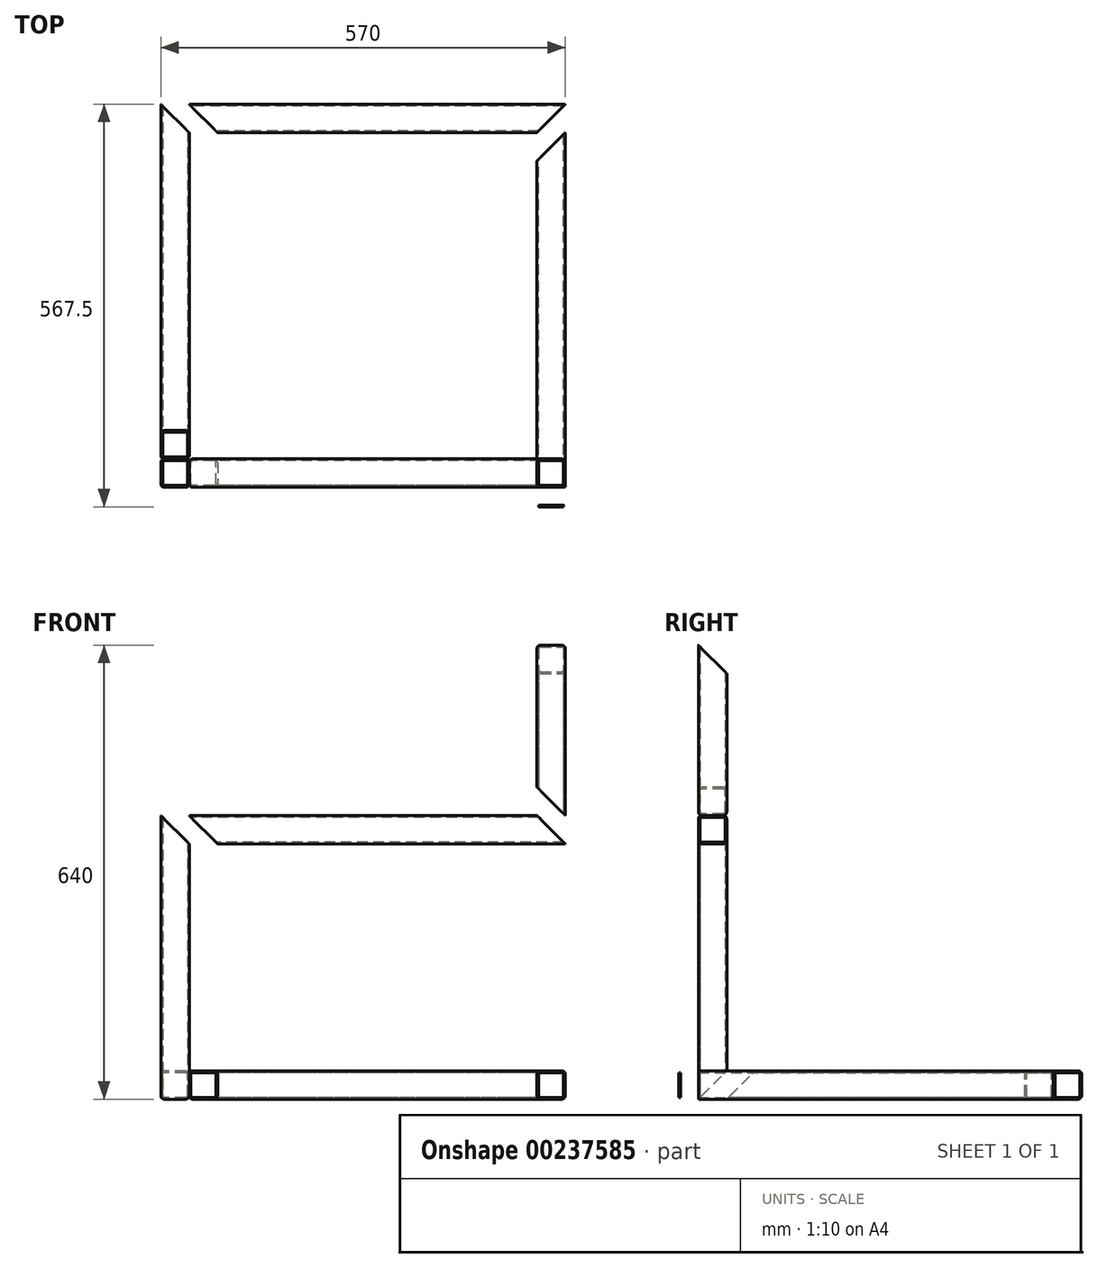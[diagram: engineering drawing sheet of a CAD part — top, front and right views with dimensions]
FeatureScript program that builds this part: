
annotation { "Feature Type Name" : "Feature", "Feature Type Description" : "" }
export const myFeature = defineFeature(function(context is Context, id is Id, definition is map)
    precondition{}
    {
        {
            var Q0;
            Q0=qCreatedBy(makeId("Front.planeOp"),FACE);
            var sketch = newSketch(context, id + "F0", { "sketchPlane" : qUnion([Q0])});
            skLineSegment(sketch, "E0.bottom", {"start": v(5, 0) * mm, "end": v(35, 0) * mm});
            skLineSegment(sketch, "E0.top", {"start": v(5, 40) * mm, "end": v(35, 40) * mm});
            skLineSegment(sketch, "E0.left", {"start": v(0, 5) * mm, "end": v(0, 35) * mm});
            skLineSegment(sketch, "E0.right", {"start": v(40, 5) * mm, "end": v(40, 35) * mm});
            skPoint(sketch, "E1.visualSharp", {"position": v(0, 0) * mm});
            skArc(sketch, "E1.filletArc", {"start": v(0, 5) * mm, "mid": v(1.46, 1.46) * mm, "end": v(5, 0) * mm});
            skPoint(sketch, "E2.visualSharp", {"position": v(0, 40) * mm});
            skArc(sketch, "E2.filletArc", {"start": v(5, 40) * mm, "mid": v(1.46, 38.54) * mm, "end": v(0, 35) * mm});
            skPoint(sketch, "E3.visualSharp", {"position": v(40, 40) * mm});
            skArc(sketch, "E3.filletArc", {"start": v(40, 35) * mm, "mid": v(38.54, 38.54) * mm, "end": v(35, 40) * mm});
            skPoint(sketch, "E4.visualSharp", {"position": v(40, 0) * mm});
            skArc(sketch, "E4.filletArc", {"start": v(35, 0) * mm, "mid": v(38.54, 1.46) * mm, "end": v(40, 5) * mm});
            skLineSegment(sketch, "E5.0", {"start": v(5, 37.5) * mm, "end": v(35, 37.5) * mm});
            skLineSegment(sketch, "E5.1", {"start": v(2.5, 5) * mm, "end": v(2.5, 35) * mm});
            skLineSegment(sketch, "E5.2", {"start": v(5, 2.5) * mm, "end": v(35, 2.5) * mm});
            skLineSegment(sketch, "E5.3", {"start": v(37.5, 5) * mm, "end": v(37.5, 35) * mm});
            skPoint(sketch, "E6.visualSharp", {"position": v(37.5, 37.5) * mm});
            skArc(sketch, "E6.filletArc", {"start": v(37.5, 35) * mm, "mid": v(36.77, 36.77) * mm, "end": v(35, 37.5) * mm});
            skPoint(sketch, "E7.visualSharp", {"position": v(2.5, 37.5) * mm});
            skArc(sketch, "E7.filletArc", {"start": v(5, 37.5) * mm, "mid": v(3.23, 36.77) * mm, "end": v(2.5, 35) * mm});
            skPoint(sketch, "E8.visualSharp", {"position": v(2.5, 2.5) * mm});
            skArc(sketch, "E8.filletArc", {"start": v(2.5, 5) * mm, "mid": v(3.23, 3.23) * mm, "end": v(5, 2.5) * mm});
            skPoint(sketch, "E9.visualSharp", {"position": v(37.5, 2.5) * mm});
            skArc(sketch, "E9.filletArc", {"start": v(35, 2.5) * mm, "mid": v(36.77, 3.23) * mm, "end": v(37.5, 5) * mm});
            skSolve(sketch);
        }
        {
            var Q0;
            Q0=makeQuery(id+"F0.imprint","IMPRINT",FACE,{"disambiguationData":[TD([[makeQuery(id+"F0.imprint","IMPRINT",EDGE,{"derivedFrom":sQuery(id+"F0.wireOp",EDGE,"E0.bottom")}),1.0]])]});
            extrude(context, id + "F1", {"entities" : qUnion([Q0]), "oppositeDirection" : true, "depth" : 500 * mm});
        }
        {
            var Q0;
            Q0=makeQuery(id+"F1.opExtrude","SWEPT_FACE",FACE,{"disambiguationData":[OSD([sQuery(id+"F0.wireOp",EDGE,"E0.top")])]});
            var sketch = newSketch(context, id + "F2", { "sketchPlane" : qUnion([Q0])});
            skLineSegment(sketch, "E10", {"start": v(40, 500) * mm, "end": v(0, 500) * mm});
            skLineSegment(sketch, "E11", {"start": v(0, 500) * mm, "end": v(0, 460) * mm});
            skLineSegment(sketch, "E12", {"start": v(0, 460) * mm, "end": v(40, 500) * mm});
            skSolve(sketch);
        }
        {
            var Q0;
            Q0 = qSketchRegion(id + "F2", true);
            extrude(context, id + "F3", {"entities" : qUnion([Q0]), "operationType" : NewBodyOperationType.REMOVE, "endBound" : BoundingType.THROUGH_ALL, "oppositeDirection" : true, "depth" : 25 * mm});
        }
        {
            var Q0;
            Q0=qCreatedBy(makeId("Front.planeOp"),FACE);
            var sketch = newSketch(context, id + "F4", { "sketchPlane" : qUnion([Q0])});
            skLineSegment(sketch, "E13.bottom", {"start": v(-227.11, 224.23) * mm, "end": v(-197.11, 224.23) * mm});
            skLineSegment(sketch, "E13.top", {"start": v(-227.11, 264.23) * mm, "end": v(-197.11, 264.23) * mm});
            skLineSegment(sketch, "E13.left", {"start": v(-232.11, 229.23) * mm, "end": v(-232.11, 259.23) * mm});
            skLineSegment(sketch, "E13.right", {"start": v(-192.11, 229.23) * mm, "end": v(-192.11, 259.23) * mm});
            skPoint(sketch, "E14.visualSharp", {"position": v(-232.11, 224.23) * mm});
            skArc(sketch, "E14.filletArc", {"start": v(-232.11, 229.23) * mm, "mid": v(-230.65, 225.7) * mm, "end": v(-227.11, 224.23) * mm});
            skPoint(sketch, "E15.visualSharp", {"position": v(-232.11, 264.23) * mm});
            skArc(sketch, "E15.filletArc", {"start": v(-227.11, 264.23) * mm, "mid": v(-230.65, 262.77) * mm, "end": v(-232.11, 259.23) * mm});
            skPoint(sketch, "E16.visualSharp", {"position": v(-192.11, 264.23) * mm});
            skArc(sketch, "E16.filletArc", {"start": v(-192.11, 259.23) * mm, "mid": v(-193.57, 262.77) * mm, "end": v(-197.11, 264.23) * mm});
            skPoint(sketch, "E17.visualSharp", {"position": v(-192.11, 224.23) * mm});
            skArc(sketch, "E17.filletArc", {"start": v(-197.11, 224.23) * mm, "mid": v(-193.57, 225.7) * mm, "end": v(-192.11, 229.23) * mm});
            skLineSegment(sketch, "E18.0", {"start": v(-227.11, 261.73) * mm, "end": v(-197.11, 261.73) * mm});
            skLineSegment(sketch, "E18.1", {"start": v(-229.61, 229.23) * mm, "end": v(-229.61, 259.23) * mm});
            skLineSegment(sketch, "E18.2", {"start": v(-227.11, 226.73) * mm, "end": v(-197.11, 226.73) * mm});
            skLineSegment(sketch, "E18.3", {"start": v(-194.61, 229.23) * mm, "end": v(-194.61, 259.23) * mm});
            skPoint(sketch, "E19.visualSharp", {"position": v(-194.61, 261.73) * mm});
            skArc(sketch, "E19.filletArc", {"start": v(-194.61, 259.23) * mm, "mid": v(-195.34, 261) * mm, "end": v(-197.11, 261.73) * mm});
            skPoint(sketch, "E20.visualSharp", {"position": v(-229.61, 261.73) * mm});
            skArc(sketch, "E20.filletArc", {"start": v(-227.11, 261.73) * mm, "mid": v(-228.88, 261) * mm, "end": v(-229.61, 259.23) * mm});
            skPoint(sketch, "E21.visualSharp", {"position": v(-229.61, 226.73) * mm});
            skArc(sketch, "E21.filletArc", {"start": v(-229.61, 229.23) * mm, "mid": v(-228.88, 227.47) * mm, "end": v(-227.11, 226.73) * mm});
            skPoint(sketch, "E22.visualSharp", {"position": v(-194.61, 226.73) * mm});
            skArc(sketch, "E22.filletArc", {"start": v(-197.11, 226.73) * mm, "mid": v(-195.34, 227.47) * mm, "end": v(-194.61, 229.23) * mm});
            skSolve(sketch);
        }
        {
            var Q0;
            Q0=makeQuery(id+"F4.imprint","IMPRINT",FACE,{"disambiguationData":[TD([[makeQuery(id+"F4.imprint","IMPRINT",EDGE,{"derivedFrom":sQuery(id+"F4.wireOp",EDGE,"E13.bottom")}),1.0]])]});
            extrude(context, id + "F5", {"entities" : qUnion([Q0]), "oppositeDirection" : true, "depth" : 530 * mm});
        }
        {
            var Q0;
            Q0=makeQuery(id+"F5.opExtrude","SWEPT_FACE",FACE,{"disambiguationData":[OSD([sQuery(id+"F4.wireOp",EDGE,"E13.top")])]});
            var sketch = newSketch(context, id + "F6", { "sketchPlane" : qUnion([Q0])});
            skLineSegment(sketch, "E23", {"start": v(-232.11, 0) * mm, "end": v(-232.11, 40) * mm});
            skLineSegment(sketch, "E24", {"start": v(-232.11, 0) * mm, "end": v(-192.11, 0) * mm});
            skLineSegment(sketch, "E25", {"start": v(-192.11, 0) * mm, "end": v(-232.11, 40) * mm});
            skLineSegment(sketch, "E26", {"start": v(-227.11, 265) * mm, "end": v(-176.46, 265) * mm, "construction": true});
            skLineSegment(sketch, "E27.MirrorCS", {"start": v(-232.11, 530) * mm, "end": v(-192.11, 530) * mm});
            skLineSegment(sketch, "E28.MirrorCS", {"start": v(-232.11, 530) * mm, "end": v(-232.11, 490) * mm});
            skLineSegment(sketch, "E29.MirrorCS", {"start": v(-192.11, 530) * mm, "end": v(-232.11, 490) * mm});
            skSolve(sketch);
        }
        {
            var Q0;
            Q0 = qSketchRegion(id + "F6", true);
            extrude(context, id + "F7", {"entities" : qUnion([Q0]), "operationType" : NewBodyOperationType.REMOVE, "endBound" : BoundingType.THROUGH_ALL, "oppositeDirection" : true, "depth" : 25 * mm});
        }
        {
            var Q0;
            Q0=makeQuery(id+"F1.opExtrude","SWEPT_BODY",BODY,{"disambiguationData":[OSD([sQuery(id+"F0.wireOp",EDGE,"E0.bottom"),sQuery(id+"F0.wireOp",EDGE,"E0.top"),sQuery(id+"F0.wireOp",EDGE,"E0.left"),sQuery(id+"F0.wireOp",EDGE,"E0.right"),sQuery(id+"F0.wireOp",EDGE,"E1.filletArc"),sQuery(id+"F0.wireOp",EDGE,"E2.filletArc"),sQuery(id+"F0.wireOp",EDGE,"E3.filletArc"),sQuery(id+"F0.wireOp",EDGE,"E4.filletArc"),sQuery(id+"F0.wireOp",EDGE,"E5.0"),sQuery(id+"F0.wireOp",EDGE,"E5.1"),sQuery(id+"F0.wireOp",EDGE,"E5.2"),sQuery(id+"F0.wireOp",EDGE,"E5.3"),sQuery(id+"F0.wireOp",EDGE,"E6.filletArc"),sQuery(id+"F0.wireOp",EDGE,"E7.filletArc"),sQuery(id+"F0.wireOp",EDGE,"E8.filletArc"),sQuery(id+"F0.wireOp",EDGE,"E9.filletArc")])]});
            transform(context, id + "F8", {"entities" : qUnion([Q0]), "transformType" : TransformType.TRANSLATION_3D, "dx" : -219 * mm, "dy" : 0 * mm, "dz" : 7 * mm, "makeCopy" : true});
        }
        {
            var Q0;
            Q0=makeQuery(id+"F8.opPattern","COPY",FACE,{"derivedFrom":makeQuery(id+"F1.opExtrude","SWEPT_FACE",FACE,{"disambiguationData":[OSD([sQuery(id+"F0.wireOp",EDGE,"E0.left")])]}),"instanceName":"1"});
            var sketch = newSketch(context, id + "F9", { "sketchPlane" : qUnion([Q0])});
            skLineSegment(sketch, "E30", {"start": v(0, 7) * mm, "end": v(0, 47) * mm});
            skLineSegment(sketch, "E31", {"start": v(0, 47) * mm, "end": v(-40, 7) * mm});
            skLineSegment(sketch, "E32", {"start": v(-40, 7) * mm, "end": v(0, 7) * mm});
            skSolve(sketch);
        }
        {
            var Q0;
            Q0 = qSketchRegion(id + "F9", true);
            extrude(context, id + "F10", {"entities" : qUnion([Q0]), "operationType" : NewBodyOperationType.REMOVE, "endBound" : BoundingType.THROUGH_ALL, "oppositeDirection" : true, "depth" : 25 * mm});
        }
        {
            var Q0;
            Q0=makeQuery(id+"F1.opExtrude","SWEPT_BODY",BODY,{"disambiguationData":[OSD([sQuery(id+"F0.wireOp",EDGE,"E0.bottom"),sQuery(id+"F0.wireOp",EDGE,"E0.top"),sQuery(id+"F0.wireOp",EDGE,"E0.left"),sQuery(id+"F0.wireOp",EDGE,"E0.right"),sQuery(id+"F0.wireOp",EDGE,"E1.filletArc"),sQuery(id+"F0.wireOp",EDGE,"E2.filletArc"),sQuery(id+"F0.wireOp",EDGE,"E3.filletArc"),sQuery(id+"F0.wireOp",EDGE,"E4.filletArc"),sQuery(id+"F0.wireOp",EDGE,"E5.0"),sQuery(id+"F0.wireOp",EDGE,"E5.1"),sQuery(id+"F0.wireOp",EDGE,"E5.2"),sQuery(id+"F0.wireOp",EDGE,"E5.3"),sQuery(id+"F0.wireOp",EDGE,"E6.filletArc"),sQuery(id+"F0.wireOp",EDGE,"E7.filletArc"),sQuery(id+"F0.wireOp",EDGE,"E8.filletArc"),sQuery(id+"F0.wireOp",EDGE,"E9.filletArc")])]});
            transform(context, id + "F11", {"entities" : qUnion([Q0]), "transformType" : TransformType.TRANSLATION_3D, "dx" : 124 * mm, "dy" : 2 * mm, "dz" : 116 * mm, "makeCopy" : true});
        }
        {
            var Q0;
            Q0=makeQuery(id+"F11.opPattern","COPY",BODY,{"derivedFrom":makeQuery(id+"F1.opExtrude","SWEPT_BODY",BODY,{"disambiguationData":[OSD([sQuery(id+"F0.wireOp",EDGE,"E0.bottom"),sQuery(id+"F0.wireOp",EDGE,"E0.top"),sQuery(id+"F0.wireOp",EDGE,"E0.left"),sQuery(id+"F0.wireOp",EDGE,"E0.right"),sQuery(id+"F0.wireOp",EDGE,"E1.filletArc"),sQuery(id+"F0.wireOp",EDGE,"E2.filletArc"),sQuery(id+"F0.wireOp",EDGE,"E3.filletArc"),sQuery(id+"F0.wireOp",EDGE,"E4.filletArc"),sQuery(id+"F0.wireOp",EDGE,"E5.0"),sQuery(id+"F0.wireOp",EDGE,"E5.1"),sQuery(id+"F0.wireOp",EDGE,"E5.2"),sQuery(id+"F0.wireOp",EDGE,"E5.3"),sQuery(id+"F0.wireOp",EDGE,"E6.filletArc"),sQuery(id+"F0.wireOp",EDGE,"E7.filletArc"),sQuery(id+"F0.wireOp",EDGE,"E8.filletArc"),sQuery(id+"F0.wireOp",EDGE,"E9.filletArc")])]}),"instanceName":"1"});
            deleteBodies(context, id + "F12", {"entities" : qUnion([Q0])});
        }
        {
            var Q0;
            Q0=qCreatedBy(makeId("Top.planeOp"),FACE);
            var sketch = newSketch(context, id + "F13", { "sketchPlane" : qUnion([Q0])});
            skLineSegment(sketch, "E33.bottom", {"start": v(188.38, -1.2) * mm, "end": v(218.38, -1.2) * mm});
            skLineSegment(sketch, "E33.top", {"start": v(188.38, 38.8) * mm, "end": v(218.38, 38.8) * mm});
            skLineSegment(sketch, "E33.left", {"start": v(183.38, 3.8) * mm, "end": v(183.38, 33.8) * mm});
            skLineSegment(sketch, "E33.right", {"start": v(223.38, 3.8) * mm, "end": v(223.38, 33.8) * mm});
            skPoint(sketch, "E34.visualSharp", {"position": v(183.38, -1.2) * mm});
            skArc(sketch, "E34.filletArc", {"start": v(183.38, 3.8) * mm, "mid": v(184.84, 0.27) * mm, "end": v(188.38, -1.2) * mm});
            skPoint(sketch, "E35.visualSharp", {"position": v(183.38, 38.8) * mm});
            skArc(sketch, "E35.filletArc", {"start": v(188.38, 38.8) * mm, "mid": v(184.84, 37.34) * mm, "end": v(183.38, 33.8) * mm});
            skPoint(sketch, "E36.visualSharp", {"position": v(223.38, 38.8) * mm});
            skArc(sketch, "E36.filletArc", {"start": v(223.38, 33.8) * mm, "mid": v(221.91, 37.34) * mm, "end": v(218.38, 38.8) * mm});
            skPoint(sketch, "E37.visualSharp", {"position": v(223.38, -1.2) * mm});
            skArc(sketch, "E37.filletArc", {"start": v(218.38, -1.2) * mm, "mid": v(221.91, 0.27) * mm, "end": v(223.38, 3.8) * mm});
            skLineSegment(sketch, "E38.0", {"start": v(188.38, 36.3) * mm, "end": v(218.38, 36.3) * mm});
            skLineSegment(sketch, "E38.1", {"start": v(185.88, 3.8) * mm, "end": v(185.88, 33.8) * mm});
            skLineSegment(sketch, "E38.2", {"start": v(188.38, 1.3) * mm, "end": v(218.38, 1.3) * mm});
            skLineSegment(sketch, "E38.3", {"start": v(220.88, 3.8) * mm, "end": v(220.88, 33.8) * mm});
            skPoint(sketch, "E39.visualSharp", {"position": v(220.88, 36.3) * mm});
            skArc(sketch, "E39.filletArc", {"start": v(220.88, 33.8) * mm, "mid": v(220.15, 35.58) * mm, "end": v(218.38, 36.3) * mm});
            skPoint(sketch, "E40.visualSharp", {"position": v(185.88, 36.3) * mm});
            skArc(sketch, "E40.filletArc", {"start": v(188.38, 36.3) * mm, "mid": v(186.61, 35.58) * mm, "end": v(185.88, 33.8) * mm});
            skPoint(sketch, "E41.visualSharp", {"position": v(185.88, 1.3) * mm});
            skArc(sketch, "E41.filletArc", {"start": v(185.88, 3.8) * mm, "mid": v(186.61, 2.04) * mm, "end": v(188.38, 1.3) * mm});
            skPoint(sketch, "E42.visualSharp", {"position": v(220.88, 1.3) * mm});
            skArc(sketch, "E42.filletArc", {"start": v(218.38, 1.3) * mm, "mid": v(220.15, 2.04) * mm, "end": v(220.88, 3.8) * mm});
            skSolve(sketch);
        }
        {
            var Q0;
            Q0=makeQuery(id+"F13.imprint","IMPRINT",FACE,{"disambiguationData":[TD([[makeQuery(id+"F13.imprint","IMPRINT",EDGE,{"derivedFrom":sQuery(id+"F13.wireOp",EDGE,"E33.bottom")}),1.0]])]});
            extrude(context, id + "F14", {"entities" : qUnion([Q0]), "depth" : 400 * mm});
        }
        {
            var Q0;
            Q0=makeQuery(id+"F14.opExtrude","SWEPT_FACE",FACE,{"disambiguationData":[OSD([sQuery(id+"F13.wireOp",EDGE,"E33.right")])]});
            var sketch = newSketch(context, id + "F15", { "sketchPlane" : qUnion([Q0])});
            skLineSegment(sketch, "E43", {"start": v(38.8, 0) * mm, "end": v(-1.2, 0) * mm});
            skLineSegment(sketch, "E44", {"start": v(38.8, 0) * mm, "end": v(38.8, 40) * mm});
            skLineSegment(sketch, "E45", {"start": v(38.8, 40) * mm, "end": v(-1.2, 0) * mm});
            skSolve(sketch);
        }
        {
            var Q0;
            Q0 = qSketchRegion(id + "F15", true);
            extrude(context, id + "F16", {"entities" : qUnion([Q0]), "operationType" : NewBodyOperationType.REMOVE, "endBound" : BoundingType.THROUGH_ALL, "oppositeDirection" : true, "depth" : 23.9 * mm});
        }
        {
            var Q0;
            Q0=makeQuery(id+"F14.opExtrude","SWEPT_FACE",FACE,{"disambiguationData":[OSD([sQuery(id+"F13.wireOp",EDGE,"E33.bottom")])]});
            var sketch = newSketch(context, id + "F17", { "sketchPlane" : qUnion([Q0])});
            skLineSegment(sketch, "E46", {"start": v(183.38, 400) * mm, "end": v(223.38, 400) * mm});
            skLineSegment(sketch, "E47", {"start": v(223.38, 400) * mm, "end": v(223.38, 360) * mm});
            skLineSegment(sketch, "E48", {"start": v(223.38, 360) * mm, "end": v(183.38, 400) * mm});
            skSolve(sketch);
        }
        {
            var Q0;
            Q0 = qSketchRegion(id + "F17", true);
            extrude(context, id + "F18", {"entities" : qUnion([Q0]), "operationType" : NewBodyOperationType.REMOVE, "endBound" : BoundingType.THROUGH_ALL, "oppositeDirection" : true, "depth" : 25 * mm});
        }
        {
            var Q0;
            Q0=makeQuery(id+"F14.opExtrude","SWEPT_FACE",FACE,{"disambiguationData":[OSD([sQuery(id+"F13.wireOp",EDGE,"E33.right")])]});
            var sketch = newSketch(context, id + "F19", { "sketchPlane" : qUnion([Q0])});
            skLineSegment(sketch, "E49.bottom", {"start": v(3.8, 360) * mm, "end": v(33.8, 360) * mm});
            skLineSegment(sketch, "E49.top", {"start": v(3.8, 400) * mm, "end": v(33.8, 400) * mm});
            skLineSegment(sketch, "E49.left", {"start": v(-1.2, 365) * mm, "end": v(-1.2, 395) * mm});
            skLineSegment(sketch, "E49.right", {"start": v(38.8, 365) * mm, "end": v(38.8, 395) * mm});
            skPoint(sketch, "E50.visualSharp", {"position": v(-1.2, 360) * mm});
            skArc(sketch, "E50.filletArc", {"start": v(-1.2, 365) * mm, "mid": v(0.27, 361.46) * mm, "end": v(3.8, 360) * mm});
            skPoint(sketch, "E51.visualSharp", {"position": v(-1.2, 400) * mm});
            skArc(sketch, "E51.filletArc", {"start": v(3.8, 400) * mm, "mid": v(0.27, 398.54) * mm, "end": v(-1.2, 395) * mm});
            skPoint(sketch, "E52.visualSharp", {"position": v(38.8, 400) * mm});
            skArc(sketch, "E52.filletArc", {"start": v(38.8, 395) * mm, "mid": v(37.34, 398.54) * mm, "end": v(33.8, 400) * mm});
            skPoint(sketch, "E53.visualSharp", {"position": v(38.8, 360) * mm});
            skArc(sketch, "E53.filletArc", {"start": v(33.8, 360) * mm, "mid": v(37.34, 361.46) * mm, "end": v(38.8, 365) * mm});
            skLineSegment(sketch, "E54.0", {"start": v(3.8, 397.5) * mm, "end": v(33.8, 397.5) * mm});
            skLineSegment(sketch, "E54.1", {"start": v(1.3, 365) * mm, "end": v(1.3, 395) * mm});
            skLineSegment(sketch, "E54.2", {"start": v(3.8, 362.5) * mm, "end": v(33.8, 362.5) * mm});
            skLineSegment(sketch, "E54.3", {"start": v(36.3, 365) * mm, "end": v(36.3, 395) * mm});
            skPoint(sketch, "E55.visualSharp", {"position": v(36.3, 397.5) * mm});
            skArc(sketch, "E55.filletArc", {"start": v(36.3, 395) * mm, "mid": v(35.58, 396.77) * mm, "end": v(33.8, 397.5) * mm});
            skPoint(sketch, "E56.visualSharp", {"position": v(1.3, 397.5) * mm});
            skArc(sketch, "E56.filletArc", {"start": v(3.8, 397.5) * mm, "mid": v(2.04, 396.77) * mm, "end": v(1.3, 395) * mm});
            skPoint(sketch, "E57.visualSharp", {"position": v(1.3, 362.5) * mm});
            skArc(sketch, "E57.filletArc", {"start": v(1.3, 365) * mm, "mid": v(2.04, 363.23) * mm, "end": v(3.8, 362.5) * mm});
            skPoint(sketch, "E58.visualSharp", {"position": v(36.3, 362.5) * mm});
            skArc(sketch, "E58.filletArc", {"start": v(33.8, 362.5) * mm, "mid": v(35.58, 363.23) * mm, "end": v(36.3, 365) * mm});
            skSolve(sketch);
        }
        {
            var Q0;
            Q0 = qSketchRegion(id + "F19", true);
            extrude(context, id + "F20", {"entities" : qUnion([Q0]), "depth" : 530 * mm});
        }
        {
            var Q0;
            Q0=makeQuery(id+"F20.opExtrude","SWEPT_FACE",FACE,{"disambiguationData":[OSD([sQuery(id+"F19.wireOp",EDGE,"E49.left")])]});
            var sketch = newSketch(context, id + "F21", { "sketchPlane" : qUnion([Q0])});
            skLineSegment(sketch, "E59", {"start": v(223.38, 400) * mm, "end": v(223.38, 360) * mm});
            skLineSegment(sketch, "E60", {"start": v(753.38, 400) * mm, "end": v(713.38, 400) * mm});
            skLineSegment(sketch, "E61", {"start": v(713.38, 400) * mm, "end": v(753.38, 360) * mm});
            skLineSegment(sketch, "E62", {"start": v(753.38, 360) * mm, "end": v(753.38, 400) * mm});
            skLineSegment(sketch, "E63", {"start": v(223.38, 360) * mm, "end": v(263.38, 360) * mm});
            skLineSegment(sketch, "E64", {"start": v(263.38, 360) * mm, "end": v(223.38, 400) * mm});
            skSolve(sketch);
        }
        {
            var Q0;
            Q0 = qSketchRegion(id + "F21", true);
            extrude(context, id + "F22", {"entities" : qUnion([Q0]), "operationType" : NewBodyOperationType.REMOVE, "endBound" : BoundingType.THROUGH_ALL, "oppositeDirection" : true, "depth" : 25 * mm});
        }
        {
            var Q0;
            Q0=makeQuery(id+"F20.opExtrude","SWEPT_FACE",FACE,{"disambiguationData":[OSD([sQuery(id+"F19.wireOp",EDGE,"E49.top")])]});
            var sketch = newSketch(context, id + "F23", { "sketchPlane" : qUnion([Q0])});
            skLineSegment(sketch, "E65.bottom", {"start": v(718.38, -1.2) * mm, "end": v(748.38, -1.2) * mm});
            skLineSegment(sketch, "E65.top", {"start": v(718.38, 38.8) * mm, "end": v(748.38, 38.8) * mm});
            skLineSegment(sketch, "E65.left", {"start": v(713.38, 3.8) * mm, "end": v(713.38, 33.8) * mm});
            skLineSegment(sketch, "E65.right", {"start": v(753.38, 3.8) * mm, "end": v(753.38, 33.8) * mm});
            skPoint(sketch, "E66.visualSharp", {"position": v(713.38, -1.2) * mm});
            skArc(sketch, "E66.filletArc", {"start": v(713.38, 3.8) * mm, "mid": v(714.84, 0.27) * mm, "end": v(718.38, -1.2) * mm});
            skPoint(sketch, "E67.visualSharp", {"position": v(713.38, 38.8) * mm});
            skArc(sketch, "E67.filletArc", {"start": v(718.38, 38.8) * mm, "mid": v(714.84, 37.34) * mm, "end": v(713.38, 33.8) * mm});
            skPoint(sketch, "E68.visualSharp", {"position": v(753.38, 38.8) * mm});
            skArc(sketch, "E68.filletArc", {"start": v(753.38, 33.8) * mm, "mid": v(751.91, 37.34) * mm, "end": v(748.38, 38.8) * mm});
            skPoint(sketch, "E69.visualSharp", {"position": v(753.38, -1.2) * mm});
            skArc(sketch, "E69.filletArc", {"start": v(748.38, -1.2) * mm, "mid": v(751.91, 0.27) * mm, "end": v(753.38, 3.8) * mm});
            skLineSegment(sketch, "E70.0", {"start": v(718.38, 36.3) * mm, "end": v(748.38, 36.3) * mm});
            skLineSegment(sketch, "E70.1", {"start": v(715.88, 3.8) * mm, "end": v(715.88, 33.8) * mm});
            skLineSegment(sketch, "E70.2", {"start": v(718.38, 1.3) * mm, "end": v(748.38, 1.3) * mm});
            skLineSegment(sketch, "E70.3", {"start": v(750.88, 3.8) * mm, "end": v(750.88, 33.8) * mm});
            skPoint(sketch, "E71.visualSharp", {"position": v(750.88, 36.3) * mm});
            skArc(sketch, "E71.filletArc", {"start": v(750.88, 33.8) * mm, "mid": v(750.15, 35.58) * mm, "end": v(748.38, 36.3) * mm});
            skPoint(sketch, "E72.visualSharp", {"position": v(715.88, 36.3) * mm});
            skArc(sketch, "E72.filletArc", {"start": v(718.38, 36.3) * mm, "mid": v(716.61, 35.58) * mm, "end": v(715.88, 33.8) * mm});
            skPoint(sketch, "E73.visualSharp", {"position": v(715.88, 1.3) * mm});
            skArc(sketch, "E73.filletArc", {"start": v(715.88, 3.8) * mm, "mid": v(716.61, 2.04) * mm, "end": v(718.38, 1.3) * mm});
            skPoint(sketch, "E74.visualSharp", {"position": v(750.88, 1.3) * mm});
            skArc(sketch, "E74.filletArc", {"start": v(748.38, 1.3) * mm, "mid": v(750.15, 2.04) * mm, "end": v(750.88, 3.8) * mm});
            skSolve(sketch);
        }
        {
            var Q0;
            Q0 = qSketchRegion(id + "F23", true);
            extrude(context, id + "F24", {"entities" : qUnion([Q0]), "depth" : 240 * mm});
        }
        {
            var Q0;
            Q0=makeQuery(id+"F24.opExtrude","SWEPT_FACE",FACE,{"disambiguationData":[OSD([sQuery(id+"F23.wireOp",EDGE,"E65.bottom")])]});
            var sketch = newSketch(context, id + "F25", { "sketchPlane" : qUnion([Q0])});
            skLineSegment(sketch, "E75", {"start": v(753.38, 400) * mm, "end": v(713.38, 400) * mm});
            skLineSegment(sketch, "E76", {"start": v(713.38, 400) * mm, "end": v(713.38, 440) * mm});
            skLineSegment(sketch, "E77", {"start": v(713.38, 440) * mm, "end": v(753.38, 400) * mm});
            skSolve(sketch);
        }
        {
            var Q0;
            Q0 = qSketchRegion(id + "F25", true);
            extrude(context, id + "F26", {"entities" : qUnion([Q0]), "operationType" : NewBodyOperationType.REMOVE, "endBound" : BoundingType.THROUGH_ALL, "oppositeDirection" : true, "depth" : 25 * mm});
        }
        {
            var Q0;
            Q0=makeQuery(id+"F24.opExtrude","SWEPT_FACE",FACE,{"disambiguationData":[OSD([sQuery(id+"F23.wireOp",EDGE,"E65.right")])]});
            var sketch = newSketch(context, id + "F27", { "sketchPlane" : qUnion([Q0])});
            skLineSegment(sketch, "E78", {"start": v(-1.2, 640) * mm, "end": v(38.8, 640) * mm});
            skLineSegment(sketch, "E79", {"start": v(38.8, 640) * mm, "end": v(38.8, 600) * mm});
            skLineSegment(sketch, "E80", {"start": v(38.8, 600) * mm, "end": v(-1.2, 640) * mm});
            skSolve(sketch);
        }
        {
            var Q0;
            Q0 = qSketchRegion(id + "F27", true);
            extrude(context, id + "F28", {"entities" : qUnion([Q0]), "operationType" : NewBodyOperationType.REMOVE, "endBound" : BoundingType.THROUGH_ALL, "oppositeDirection" : true, "depth" : 25 * mm});
        }
        {
            var Q0;
            Q0=makeQuery(id+"F24.opExtrude","SWEPT_FACE",FACE,{"disambiguationData":[OSD([sQuery(id+"F23.wireOp",EDGE,"E65.top")])]});
            var sketch = newSketch(context, id + "F29", { "sketchPlane" : qUnion([Q0])});
            skLineSegment(sketch, "E81.bottom", {"start": v(-748.38, 600) * mm, "end": v(-718.38, 600) * mm});
            skLineSegment(sketch, "E81.top", {"start": v(-748.38, 640) * mm, "end": v(-718.38, 640) * mm});
            skLineSegment(sketch, "E81.left", {"start": v(-753.38, 605) * mm, "end": v(-753.38, 635) * mm});
            skLineSegment(sketch, "E81.right", {"start": v(-713.38, 605) * mm, "end": v(-713.38, 635) * mm});
            skPoint(sketch, "E82.visualSharp", {"position": v(-753.38, 600) * mm});
            skArc(sketch, "E82.filletArc", {"start": v(-753.38, 605) * mm, "mid": v(-751.91, 601.46) * mm, "end": v(-748.38, 600) * mm});
            skPoint(sketch, "E83.visualSharp", {"position": v(-753.38, 640) * mm});
            skArc(sketch, "E83.filletArc", {"start": v(-748.38, 640) * mm, "mid": v(-751.91, 638.54) * mm, "end": v(-753.38, 635) * mm});
            skPoint(sketch, "E84.visualSharp", {"position": v(-713.38, 640) * mm});
            skArc(sketch, "E84.filletArc", {"start": v(-713.38, 635) * mm, "mid": v(-714.84, 638.54) * mm, "end": v(-718.38, 640) * mm});
            skPoint(sketch, "E85.visualSharp", {"position": v(-713.38, 600) * mm});
            skArc(sketch, "E85.filletArc", {"start": v(-718.38, 600) * mm, "mid": v(-714.84, 601.46) * mm, "end": v(-713.38, 605) * mm});
            skLineSegment(sketch, "E86.0", {"start": v(-748.38, 637.5) * mm, "end": v(-718.38, 637.5) * mm});
            skLineSegment(sketch, "E86.1", {"start": v(-750.88, 605) * mm, "end": v(-750.88, 635) * mm});
            skLineSegment(sketch, "E86.2", {"start": v(-748.38, 602.5) * mm, "end": v(-718.38, 602.5) * mm});
            skLineSegment(sketch, "E86.3", {"start": v(-715.88, 605) * mm, "end": v(-715.88, 635) * mm});
            skPoint(sketch, "E87.visualSharp", {"position": v(-715.88, 637.5) * mm});
            skArc(sketch, "E87.filletArc", {"start": v(-715.88, 635) * mm, "mid": v(-716.61, 636.77) * mm, "end": v(-718.38, 637.5) * mm});
            skPoint(sketch, "E88.visualSharp", {"position": v(-750.88, 637.5) * mm});
            skArc(sketch, "E88.filletArc", {"start": v(-748.38, 637.5) * mm, "mid": v(-750.15, 636.77) * mm, "end": v(-750.88, 635) * mm});
            skPoint(sketch, "E89.visualSharp", {"position": v(-750.88, 602.5) * mm});
            skArc(sketch, "E89.filletArc", {"start": v(-750.88, 605) * mm, "mid": v(-750.15, 603.23) * mm, "end": v(-748.38, 602.5) * mm});
            skPoint(sketch, "E90.visualSharp", {"position": v(-715.88, 602.5) * mm});
            skArc(sketch, "E90.filletArc", {"start": v(-718.38, 602.5) * mm, "mid": v(-716.61, 603.23) * mm, "end": v(-715.88, 605) * mm});
            skSolve(sketch);
        }
        {
            var Q0;
            Q0 = qSketchRegion(id + "F29", true);
            extrude(context, id + "F30", {"entities" : qUnion([Q0]), "depth" : 500 * mm});
        }
        {
            var Q0;
            Q0=makeQuery(id+"F30.opExtrude","SWEPT_FACE",FACE,{"disambiguationData":[OSD([sQuery(id+"F29.wireOp",EDGE,"E81.left")])]});
            var sketch = newSketch(context, id + "F31", { "sketchPlane" : qUnion([Q0])});
            skLineSegment(sketch, "E91", {"start": v(38.8, 640) * mm, "end": v(38.8, 600) * mm});
            skLineSegment(sketch, "E92", {"start": v(38.8, 600) * mm, "end": v(78.8, 600) * mm});
            skLineSegment(sketch, "E93", {"start": v(78.8, 600) * mm, "end": v(38.8, 640) * mm});
            skSolve(sketch);
        }
        {
            var Q0;
            Q0 = qSketchRegion(id + "F31", true);
            extrude(context, id + "F32", {"entities" : qUnion([Q0]), "operationType" : NewBodyOperationType.REMOVE, "endBound" : BoundingType.THROUGH_ALL, "oppositeDirection" : true, "depth" : 25 * mm});
        }
        {
            var Q0;
            Q0=makeQuery(id+"F30.opExtrude","SWEPT_FACE",FACE,{"disambiguationData":[OSD([sQuery(id+"F29.wireOp",EDGE,"E81.top")])]});
            var sketch = newSketch(context, id + "F33", { "sketchPlane" : qUnion([Q0])});
            skLineSegment(sketch, "E94", {"start": v(713.38, 538.8) * mm, "end": v(753.38, 538.8) * mm});
            skLineSegment(sketch, "E95", {"start": v(753.38, 538.8) * mm, "end": v(713.38, 498.8) * mm});
            skLineSegment(sketch, "E96", {"start": v(713.38, 498.8) * mm, "end": v(713.38, 538.8) * mm});
            skSolve(sketch);
        }
        {
            var Q0;
            Q0 = qSketchRegion(id + "F33", true);
            extrude(context, id + "F34", {"entities" : qUnion([Q0]), "operationType" : NewBodyOperationType.REMOVE, "endBound" : BoundingType.THROUGH_ALL, "oppositeDirection" : true, "depth" : 25 * mm});
        }
        {
            var Q0;
            Q0=makeQuery(id+"F8.opPattern","COPY",BODY,{"derivedFrom":makeQuery(id+"F1.opExtrude","SWEPT_BODY",BODY,{"disambiguationData":[OSD([sQuery(id+"F0.wireOp",EDGE,"E0.bottom"),sQuery(id+"F0.wireOp",EDGE,"E0.top"),sQuery(id+"F0.wireOp",EDGE,"E0.left"),sQuery(id+"F0.wireOp",EDGE,"E0.right"),sQuery(id+"F0.wireOp",EDGE,"E1.filletArc"),sQuery(id+"F0.wireOp",EDGE,"E2.filletArc"),sQuery(id+"F0.wireOp",EDGE,"E3.filletArc"),sQuery(id+"F0.wireOp",EDGE,"E4.filletArc"),sQuery(id+"F0.wireOp",EDGE,"E5.0"),sQuery(id+"F0.wireOp",EDGE,"E5.1"),sQuery(id+"F0.wireOp",EDGE,"E5.2"),sQuery(id+"F0.wireOp",EDGE,"E5.3"),sQuery(id+"F0.wireOp",EDGE,"E6.filletArc"),sQuery(id+"F0.wireOp",EDGE,"E7.filletArc"),sQuery(id+"F0.wireOp",EDGE,"E8.filletArc"),sQuery(id+"F0.wireOp",EDGE,"E9.filletArc")])]}),"instanceName":"1"});
            var Q1;
            Q1=makeQuery(id+"F5.opExtrude","SWEPT_BODY",BODY,{"disambiguationData":[OSD([sQuery(id+"F4.wireOp",EDGE,"E13.bottom"),sQuery(id+"F4.wireOp",EDGE,"E13.top"),sQuery(id+"F4.wireOp",EDGE,"E13.left"),sQuery(id+"F4.wireOp",EDGE,"E13.right"),sQuery(id+"F4.wireOp",EDGE,"E14.filletArc"),sQuery(id+"F4.wireOp",EDGE,"E15.filletArc"),sQuery(id+"F4.wireOp",EDGE,"E16.filletArc"),sQuery(id+"F4.wireOp",EDGE,"E17.filletArc"),sQuery(id+"F4.wireOp",EDGE,"E18.0"),sQuery(id+"F4.wireOp",EDGE,"E18.1"),sQuery(id+"F4.wireOp",EDGE,"E18.2"),sQuery(id+"F4.wireOp",EDGE,"E18.3"),sQuery(id+"F4.wireOp",EDGE,"E19.filletArc"),sQuery(id+"F4.wireOp",EDGE,"E20.filletArc"),sQuery(id+"F4.wireOp",EDGE,"E21.filletArc"),sQuery(id+"F4.wireOp",EDGE,"E22.filletArc")])]});
            var Q2;
            Q2=makeQuery(id+"F1.opExtrude","SWEPT_BODY",BODY,{"disambiguationData":[OSD([sQuery(id+"F0.wireOp",EDGE,"E0.bottom"),sQuery(id+"F0.wireOp",EDGE,"E0.top"),sQuery(id+"F0.wireOp",EDGE,"E0.left"),sQuery(id+"F0.wireOp",EDGE,"E0.right"),sQuery(id+"F0.wireOp",EDGE,"E1.filletArc"),sQuery(id+"F0.wireOp",EDGE,"E2.filletArc"),sQuery(id+"F0.wireOp",EDGE,"E3.filletArc"),sQuery(id+"F0.wireOp",EDGE,"E4.filletArc"),sQuery(id+"F0.wireOp",EDGE,"E5.0"),sQuery(id+"F0.wireOp",EDGE,"E5.1"),sQuery(id+"F0.wireOp",EDGE,"E5.2"),sQuery(id+"F0.wireOp",EDGE,"E5.3"),sQuery(id+"F0.wireOp",EDGE,"E6.filletArc"),sQuery(id+"F0.wireOp",EDGE,"E7.filletArc"),sQuery(id+"F0.wireOp",EDGE,"E8.filletArc"),sQuery(id+"F0.wireOp",EDGE,"E9.filletArc")])]});
            deleteBodies(context, id + "F35", {"entities" : qUnion([Q0, Q1, Q2])});
        }
        {
            var Q0;
            Q0=makeQuery(id+"F14.opExtrude","SWEPT_FACE",FACE,{"disambiguationData":[OSD([sQuery(id+"F13.wireOp",EDGE,"E33.top")])]});
            var sketch = newSketch(context, id + "F36", { "sketchPlane" : qUnion([Q0])});
            skLineSegment(sketch, "E97.bottom", {"start": v(-218.38, 0) * mm, "end": v(-188.38, 0) * mm});
            skLineSegment(sketch, "E97.top", {"start": v(-218.38, 40) * mm, "end": v(-188.38, 40) * mm});
            skLineSegment(sketch, "E97.left", {"start": v(-223.38, 5) * mm, "end": v(-223.38, 35) * mm});
            skLineSegment(sketch, "E97.right", {"start": v(-183.38, 5) * mm, "end": v(-183.38, 35) * mm});
            skPoint(sketch, "E98.visualSharp", {"position": v(-223.38, 0) * mm});
            skArc(sketch, "E98.filletArc", {"start": v(-223.38, 5) * mm, "mid": v(-221.91, 1.46) * mm, "end": v(-218.38, 0) * mm});
            skPoint(sketch, "E99.visualSharp", {"position": v(-223.38, 40) * mm});
            skArc(sketch, "E99.filletArc", {"start": v(-218.38, 40) * mm, "mid": v(-221.91, 38.54) * mm, "end": v(-223.38, 35) * mm});
            skPoint(sketch, "E100.visualSharp", {"position": v(-183.38, 40) * mm});
            skArc(sketch, "E100.filletArc", {"start": v(-183.38, 35) * mm, "mid": v(-184.84, 38.54) * mm, "end": v(-188.38, 40) * mm});
            skPoint(sketch, "E101.visualSharp", {"position": v(-183.38, 0) * mm});
            skArc(sketch, "E101.filletArc", {"start": v(-188.38, 0) * mm, "mid": v(-184.84, 1.46) * mm, "end": v(-183.38, 5) * mm});
            skLineSegment(sketch, "E102.0", {"start": v(-218.38, 37.5) * mm, "end": v(-188.38, 37.5) * mm});
            skLineSegment(sketch, "E102.1", {"start": v(-220.88, 5) * mm, "end": v(-220.88, 35) * mm});
            skLineSegment(sketch, "E102.2", {"start": v(-218.38, 2.5) * mm, "end": v(-188.38, 2.5) * mm});
            skLineSegment(sketch, "E102.3", {"start": v(-185.88, 5) * mm, "end": v(-185.88, 35) * mm});
            skPoint(sketch, "E103.visualSharp", {"position": v(-185.88, 37.5) * mm});
            skArc(sketch, "E103.filletArc", {"start": v(-185.88, 35) * mm, "mid": v(-186.61, 36.77) * mm, "end": v(-188.38, 37.5) * mm});
            skPoint(sketch, "E104.visualSharp", {"position": v(-220.88, 37.5) * mm});
            skArc(sketch, "E104.filletArc", {"start": v(-218.38, 37.5) * mm, "mid": v(-220.15, 36.77) * mm, "end": v(-220.88, 35) * mm});
            skPoint(sketch, "E105.visualSharp", {"position": v(-220.88, 2.5) * mm});
            skArc(sketch, "E105.filletArc", {"start": v(-220.88, 5) * mm, "mid": v(-220.15, 3.23) * mm, "end": v(-218.38, 2.5) * mm});
            skPoint(sketch, "E106.visualSharp", {"position": v(-185.88, 2.5) * mm});
            skArc(sketch, "E106.filletArc", {"start": v(-188.38, 2.5) * mm, "mid": v(-186.61, 3.23) * mm, "end": v(-185.88, 5) * mm});
            skSolve(sketch);
        }
        {
            var Q0;
            Q0=makeQuery(id+"F36.imprint","IMPRINT",FACE,{"disambiguationData":[TD([[makeQuery(id+"F36.imprint","IMPRINT",EDGE,{"derivedFrom":sQuery(id+"F36.wireOp",EDGE,"E97.bottom")}),1.0]])]});
            extrude(context, id + "F37", {"entities" : qUnion([Q0]), "depth" : 500 * mm});
        }
        {
            var Q0;
            Q0=makeQuery(id+"F37.opExtrude","SWEPT_FACE",FACE,{"disambiguationData":[OSD([sQuery(id+"F36.wireOp",EDGE,"E97.left")])]});
            var sketch = newSketch(context, id + "F38", { "sketchPlane" : qUnion([Q0])});
            skLineSegment(sketch, "E107", {"start": v(78.8, 40) * mm, "end": v(38.8, 40) * mm});
            skLineSegment(sketch, "E108", {"start": v(38.8, 40) * mm, "end": v(38.8, 0) * mm});
            skLineSegment(sketch, "E109", {"start": v(38.8, 0) * mm, "end": v(78.8, 40) * mm});
            skSolve(sketch);
        }
        {
            var Q0;
            Q0 = qSketchRegion(id + "F38", true);
            extrude(context, id + "F39", {"entities" : qUnion([Q0]), "operationType" : NewBodyOperationType.REMOVE, "endBound" : BoundingType.THROUGH_ALL, "oppositeDirection" : true, "depth" : 25 * mm});
        }
        {
            var Q0;
            Q0=makeQuery(id+"F37.opExtrude","SWEPT_FACE",FACE,{"disambiguationData":[OSD([sQuery(id+"F36.wireOp",EDGE,"E97.top")])]});
            var sketch = newSketch(context, id + "F40", { "sketchPlane" : qUnion([Q0])});
            skLineSegment(sketch, "E110", {"start": v(183.38, 538.8) * mm, "end": v(223.38, 538.8) * mm});
            skLineSegment(sketch, "E111", {"start": v(223.38, 538.8) * mm, "end": v(223.38, 498.8) * mm});
            skLineSegment(sketch, "E112", {"start": v(223.38, 498.8) * mm, "end": v(183.38, 538.8) * mm});
            skSolve(sketch);
        }
        {
            var Q0;
            Q0 = qSketchRegion(id + "F40", true);
            extrude(context, id + "F41", {"entities" : qUnion([Q0]), "operationType" : NewBodyOperationType.REMOVE, "endBound" : BoundingType.THROUGH_ALL, "oppositeDirection" : true, "depth" : 25 * mm});
        }
        {
            var Q0;
            Q0=makeQuery(id+"F37.opExtrude","SWEPT_FACE",FACE,{"disambiguationData":[OSD([sQuery(id+"F36.wireOp",EDGE,"E97.left")])]});
            var sketch = newSketch(context, id + "F42", { "sketchPlane" : qUnion([Q0])});
            skLineSegment(sketch, "E113.bottom", {"start": v(503.8, 0) * mm, "end": v(533.8, 0) * mm});
            skLineSegment(sketch, "E113.top", {"start": v(503.8, 40) * mm, "end": v(533.8, 40) * mm});
            skLineSegment(sketch, "E113.left", {"start": v(498.8, 5) * mm, "end": v(498.8, 35) * mm});
            skLineSegment(sketch, "E113.right", {"start": v(538.8, 5) * mm, "end": v(538.8, 35) * mm});
            skPoint(sketch, "E114.visualSharp", {"position": v(498.8, 0) * mm});
            skArc(sketch, "E114.filletArc", {"start": v(498.8, 5) * mm, "mid": v(500.27, 1.46) * mm, "end": v(503.8, 0) * mm});
            skPoint(sketch, "E115.visualSharp", {"position": v(498.8, 40) * mm});
            skArc(sketch, "E115.filletArc", {"start": v(503.8, 40) * mm, "mid": v(500.27, 38.54) * mm, "end": v(498.8, 35) * mm});
            skPoint(sketch, "E116.visualSharp", {"position": v(538.8, 40) * mm});
            skArc(sketch, "E116.filletArc", {"start": v(538.8, 35) * mm, "mid": v(537.34, 38.54) * mm, "end": v(533.8, 40) * mm});
            skPoint(sketch, "E117.visualSharp", {"position": v(538.8, 0) * mm});
            skArc(sketch, "E117.filletArc", {"start": v(533.8, 0) * mm, "mid": v(537.34, 1.46) * mm, "end": v(538.8, 5) * mm});
            skLineSegment(sketch, "E118.0", {"start": v(503.8, 37.5) * mm, "end": v(533.8, 37.5) * mm});
            skLineSegment(sketch, "E118.1", {"start": v(501.3, 5) * mm, "end": v(501.3, 35) * mm});
            skLineSegment(sketch, "E118.2", {"start": v(503.8, 2.5) * mm, "end": v(533.8, 2.5) * mm});
            skLineSegment(sketch, "E118.3", {"start": v(536.3, 5) * mm, "end": v(536.3, 35) * mm});
            skPoint(sketch, "E119.visualSharp", {"position": v(536.3, 37.5) * mm});
            skArc(sketch, "E119.filletArc", {"start": v(536.3, 35) * mm, "mid": v(535.58, 36.77) * mm, "end": v(533.8, 37.5) * mm});
            skPoint(sketch, "E120.visualSharp", {"position": v(501.3, 37.5) * mm});
            skArc(sketch, "E120.filletArc", {"start": v(503.8, 37.5) * mm, "mid": v(502.04, 36.77) * mm, "end": v(501.3, 35) * mm});
            skPoint(sketch, "E121.visualSharp", {"position": v(501.3, 2.5) * mm});
            skArc(sketch, "E121.filletArc", {"start": v(501.3, 5) * mm, "mid": v(502.04, 3.23) * mm, "end": v(503.8, 2.5) * mm});
            skPoint(sketch, "E122.visualSharp", {"position": v(536.3, 2.5) * mm});
            skArc(sketch, "E122.filletArc", {"start": v(533.8, 2.5) * mm, "mid": v(535.58, 3.23) * mm, "end": v(536.3, 5) * mm});
            skSolve(sketch);
        }
        {
            var Q0;
            Q0 = qSketchRegion(id + "F42", true);
            extrude(context, id + "F43", {"entities" : qUnion([Q0]), "depth" : 530 * mm});
        }
        {
            var Q0;
            Q0=makeQuery(id+"F43.opExtrude","SWEPT_FACE",FACE,{"disambiguationData":[OSD([sQuery(id+"F42.wireOp",EDGE,"E113.top")])]});
            var sketch = newSketch(context, id + "F44", { "sketchPlane" : qUnion([Q0])});
            skLineSegment(sketch, "E123", {"start": v(223.38, 538.8) * mm, "end": v(223.38, 498.8) * mm});
            skLineSegment(sketch, "E124", {"start": v(753.38, 538.8) * mm, "end": v(753.38, 498.8) * mm});
            skLineSegment(sketch, "E125", {"start": v(753.38, 498.8) * mm, "end": v(713.38, 498.8) * mm});
            skLineSegment(sketch, "E126", {"start": v(713.38, 498.8) * mm, "end": v(753.38, 538.8) * mm});
            skLineSegment(sketch, "E127", {"start": v(223.38, 498.8) * mm, "end": v(263.38, 498.8) * mm});
            skLineSegment(sketch, "E128", {"start": v(263.38, 498.8) * mm, "end": v(223.38, 538.8) * mm});
            skSolve(sketch);
        }
        {
            var Q0;
            Q0 = qSketchRegion(id + "F44", true);
            extrude(context, id + "F45", {"entities" : qUnion([Q0]), "operationType" : NewBodyOperationType.REMOVE, "endBound" : BoundingType.THROUGH_ALL, "oppositeDirection" : true, "depth" : 25 * mm});
        }
        {
            var Q0;
            Q0=makeQuery(id+"F43.opExtrude","SWEPT_FACE",FACE,{"disambiguationData":[OSD([sQuery(id+"F42.wireOp",EDGE,"E113.left")])]});
            var sketch = newSketch(context, id + "F46", { "sketchPlane" : qUnion([Q0])});
            skLineSegment(sketch, "E129.bottom", {"start": v(718.38, 0) * mm, "end": v(748.38, 0) * mm});
            skLineSegment(sketch, "E129.top", {"start": v(718.38, 40) * mm, "end": v(748.38, 40) * mm});
            skLineSegment(sketch, "E129.left", {"start": v(713.38, 5) * mm, "end": v(713.38, 35) * mm});
            skLineSegment(sketch, "E129.right", {"start": v(753.38, 5) * mm, "end": v(753.38, 35) * mm});
            skPoint(sketch, "E130.visualSharp", {"position": v(713.38, 0) * mm});
            skArc(sketch, "E130.filletArc", {"start": v(713.38, 5) * mm, "mid": v(714.84, 1.46) * mm, "end": v(718.38, 0) * mm});
            skPoint(sketch, "E131.visualSharp", {"position": v(713.38, 40) * mm});
            skArc(sketch, "E131.filletArc", {"start": v(718.38, 40) * mm, "mid": v(714.84, 38.54) * mm, "end": v(713.38, 35) * mm});
            skPoint(sketch, "E132.visualSharp", {"position": v(753.38, 40) * mm});
            skArc(sketch, "E132.filletArc", {"start": v(753.38, 35) * mm, "mid": v(751.91, 38.54) * mm, "end": v(748.38, 40) * mm});
            skPoint(sketch, "E133.visualSharp", {"position": v(753.38, 0) * mm});
            skArc(sketch, "E133.filletArc", {"start": v(748.38, 0) * mm, "mid": v(751.91, 1.46) * mm, "end": v(753.38, 5) * mm});
            skLineSegment(sketch, "E134.0", {"start": v(718.38, 37.5) * mm, "end": v(748.38, 37.5) * mm});
            skLineSegment(sketch, "E134.1", {"start": v(715.88, 5) * mm, "end": v(715.88, 35) * mm});
            skLineSegment(sketch, "E134.2", {"start": v(718.38, 2.5) * mm, "end": v(748.38, 2.5) * mm});
            skLineSegment(sketch, "E134.3", {"start": v(750.88, 5) * mm, "end": v(750.88, 35) * mm});
            skPoint(sketch, "E135.visualSharp", {"position": v(750.88, 37.5) * mm});
            skArc(sketch, "E135.filletArc", {"start": v(750.88, 35) * mm, "mid": v(750.15, 36.77) * mm, "end": v(748.38, 37.5) * mm});
            skPoint(sketch, "E136.visualSharp", {"position": v(715.88, 37.5) * mm});
            skArc(sketch, "E136.filletArc", {"start": v(718.38, 37.5) * mm, "mid": v(716.61, 36.77) * mm, "end": v(715.88, 35) * mm});
            skPoint(sketch, "E137.visualSharp", {"position": v(715.88, 2.5) * mm});
            skArc(sketch, "E137.filletArc", {"start": v(715.88, 5) * mm, "mid": v(716.61, 3.23) * mm, "end": v(718.38, 2.5) * mm});
            skPoint(sketch, "E138.visualSharp", {"position": v(750.88, 2.5) * mm});
            skArc(sketch, "E138.filletArc", {"start": v(748.38, 2.5) * mm, "mid": v(750.15, 3.23) * mm, "end": v(750.88, 5) * mm});
            skSolve(sketch);
        }
        {
            var Q0;
            Q0=makeQuery(id+"F46.imprint","IMPRINT",FACE,{"disambiguationData":[TD([[makeQuery(id+"F46.imprint","IMPRINT",EDGE,{"derivedFrom":sQuery(id+"F46.wireOp",EDGE,"E129.bottom")}),1.0]])]});
            extrude(context, id + "F47", {"entities" : qUnion([Q0]), "depth" : 500 * mm});
        }
        {
            var Q0;
            Q0=makeQuery(id+"F47.opExtrude","SWEPT_FACE",FACE,{"disambiguationData":[OSD([sQuery(id+"F46.wireOp",EDGE,"E129.top")])]});
            var sketch = newSketch(context, id + "F48", { "sketchPlane" : qUnion([Q0])});
            skLineSegment(sketch, "E139", {"start": v(753.38, 498.8) * mm, "end": v(713.38, 498.8) * mm});
            skLineSegment(sketch, "E140", {"start": v(713.38, 498.8) * mm, "end": v(713.38, 458.8) * mm});
            skLineSegment(sketch, "E141", {"start": v(713.38, 458.8) * mm, "end": v(753.38, 498.8) * mm});
            skSolve(sketch);
        }
        {
            var Q0;
            Q0 = qSketchRegion(id + "F48", true);
            extrude(context, id + "F49", {"entities" : qUnion([Q0]), "operationType" : NewBodyOperationType.REMOVE, "endBound" : BoundingType.THROUGH_ALL, "oppositeDirection" : true, "depth" : 25 * mm});
        }
        {
            var Q0;
            Q0=makeQuery(id+"F47.opExtrude","CAP_FACE",FACE,{"disambiguationData":[OSD([sQuery(id+"F46.wireOp",EDGE,"E129.bottom"),sQuery(id+"F46.wireOp",EDGE,"E129.top"),sQuery(id+"F46.wireOp",EDGE,"E129.left"),sQuery(id+"F46.wireOp",EDGE,"E129.right"),sQuery(id+"F46.wireOp",EDGE,"E130.filletArc"),sQuery(id+"F46.wireOp",EDGE,"E131.filletArc"),sQuery(id+"F46.wireOp",EDGE,"E132.filletArc"),sQuery(id+"F46.wireOp",EDGE,"E133.filletArc"),sQuery(id+"F46.wireOp",EDGE,"E134.0"),sQuery(id+"F46.wireOp",EDGE,"E134.1"),sQuery(id+"F46.wireOp",EDGE,"E134.2"),sQuery(id+"F46.wireOp",EDGE,"E134.3"),sQuery(id+"F46.wireOp",EDGE,"E135.filletArc"),sQuery(id+"F46.wireOp",EDGE,"E136.filletArc"),sQuery(id+"F46.wireOp",EDGE,"E137.filletArc"),sQuery(id+"F46.wireOp",EDGE,"E138.filletArc")])],"isStart":false});
            cPlane(context, id + "F50", {"entities" : qUnion([Q0]), "cplaneType" : CPlaneType.OFFSET, "offset" : 25 * mm, "width" : 150 * mm, "height" : 150 * mm});
        }
        {
            var Q0;
            Q0=qCreatedBy(id+"F50.planeOp",FACE);
            var sketch = newSketch(context, id + "F51", { "sketchPlane" : qUnion([Q0])});
            skLineSegment(sketch, "E142.0", {"start": v(718.38, 37.5) * mm, "end": v(748.38, 37.5) * mm});
            skLineSegment(sketch, "E142.1", {"start": v(715.88, 5) * mm, "end": v(715.88, 35) * mm});
            skLineSegment(sketch, "E142.2", {"start": v(718.38, 2.5) * mm, "end": v(748.38, 2.5) * mm});
            skLineSegment(sketch, "E142.3", {"start": v(750.88, 5) * mm, "end": v(750.88, 35) * mm});
            skPoint(sketch, "E143.visualSharp", {"position": v(750.88, 37.5) * mm});
            skArc(sketch, "E143.filletArc", {"start": v(750.88, 35) * mm, "mid": v(750.15, 36.77) * mm, "end": v(748.38, 37.5) * mm});
            skPoint(sketch, "E144.visualSharp", {"position": v(715.88, 37.5) * mm});
            skArc(sketch, "E144.filletArc", {"start": v(718.38, 37.5) * mm, "mid": v(716.61, 36.77) * mm, "end": v(715.88, 35) * mm});
            skPoint(sketch, "E145.visualSharp", {"position": v(715.88, 2.5) * mm});
            skArc(sketch, "E145.filletArc", {"start": v(715.88, 5) * mm, "mid": v(716.61, 3.23) * mm, "end": v(718.38, 2.5) * mm});
            skPoint(sketch, "E146.visualSharp", {"position": v(750.88, 2.5) * mm});
            skArc(sketch, "E146.filletArc", {"start": v(748.38, 2.5) * mm, "mid": v(750.15, 3.23) * mm, "end": v(750.88, 5) * mm});
            skSolve(sketch);
        }
        {
            var Q0;
            Q0 = qSketchRegion(id + "F51", true);
            extrude(context, id + "F52", {"entities" : qUnion([Q0]), "depth" : 2.5 * mm});
        }
        {
            var Q0;
            Q0=makeQuery(id+"F30.opExtrude","SWEPT_BODY",BODY,{"disambiguationData":[OSD([sQuery(id+"F29.wireOp",EDGE,"E81.bottom"),sQuery(id+"F29.wireOp",EDGE,"E81.top"),sQuery(id+"F29.wireOp",EDGE,"E81.left"),sQuery(id+"F29.wireOp",EDGE,"E81.right"),sQuery(id+"F29.wireOp",EDGE,"E82.filletArc"),sQuery(id+"F29.wireOp",EDGE,"E83.filletArc"),sQuery(id+"F29.wireOp",EDGE,"E84.filletArc"),sQuery(id+"F29.wireOp",EDGE,"E85.filletArc"),sQuery(id+"F29.wireOp",EDGE,"E86.0"),sQuery(id+"F29.wireOp",EDGE,"E86.1"),sQuery(id+"F29.wireOp",EDGE,"E86.2"),sQuery(id+"F29.wireOp",EDGE,"E86.3"),sQuery(id+"F29.wireOp",EDGE,"E87.filletArc"),sQuery(id+"F29.wireOp",EDGE,"E88.filletArc"),sQuery(id+"F29.wireOp",EDGE,"E89.filletArc"),sQuery(id+"F29.wireOp",EDGE,"E90.filletArc")])]});
            deleteBodies(context, id + "F53", {"entities" : qUnion([Q0])});
        }
    });
